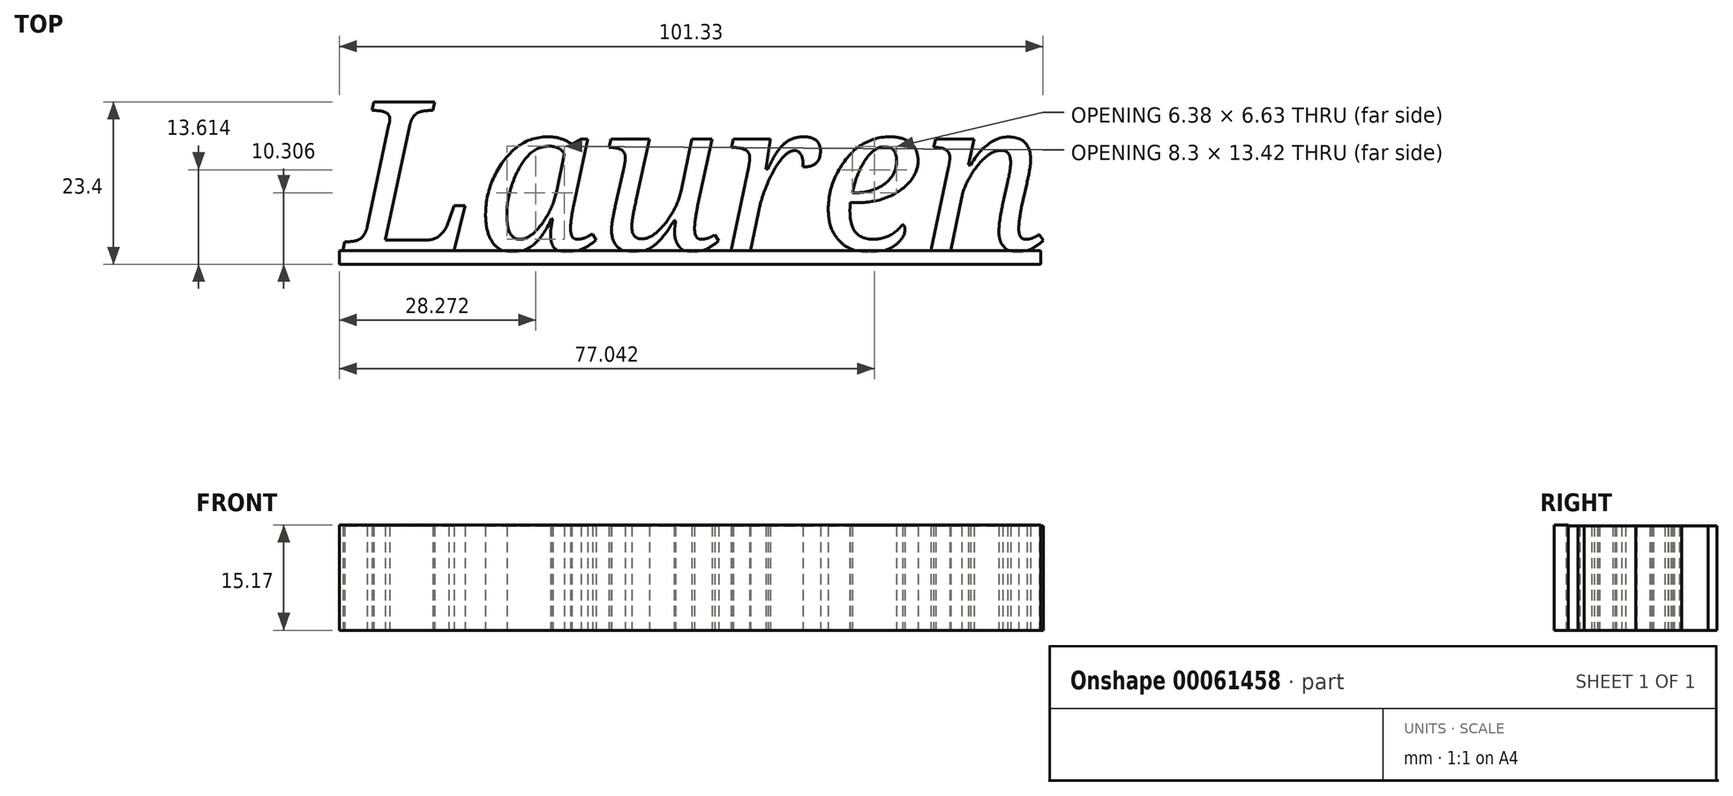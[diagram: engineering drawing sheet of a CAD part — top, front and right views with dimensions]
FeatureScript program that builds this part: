
annotation { "Feature Type Name" : "Feature", "Feature Type Description" : "" }
export const myFeature = defineFeature(function(context is Context, id is Id, definition is map)
    precondition{}
    {
        {
            var Q0;
            Q0=qCreatedBy(makeId("Top.planeOp"),FACE);
            var sketch = newSketch(context, id + "F0", { "sketchPlane" : qUnion([Q0])});
            skText(sketch, "E0", { "text": "Lauren", "fontName": "NotoSerif-Italic.ttf"});
            const initialGuessF0  = {"E0": [-0.05193, 0, 1, 0, 0.02158]};
            skSetInitialGuess(sketch, initialGuessF0);
            skSolve(sketch);
        }
        {
            var Q0;
            Q0 = qSketchRegion(id + "F0", true);
            extrude(context, id + "F1", {"entities" : qUnion([Q0]), "depth" : 15 * mm});
        }
        {
            var Q0;
            Q0=qCreatedBy(makeId("Front.planeOp"),FACE);
            var sketch = newSketch(context, id + "F2", { "sketchPlane" : qUnion([Q0])});
            skLineSegment(sketch, "E1.bottom", {"start": v(-53.03, 15.17) * mm, "end": v(47.92, 15.17) * mm});
            skLineSegment(sketch, "E1.top", {"start": v(-53.03, 0) * mm, "end": v(47.92, 0) * mm});
            skLineSegment(sketch, "E1.left", {"start": v(-53.03, 15.17) * mm, "end": v(-53.03, 0) * mm});
            skLineSegment(sketch, "E1.right", {"start": v(47.92, 15.17) * mm, "end": v(47.92, 0) * mm});
            skSolve(sketch);
        }
        {
            var Q0;
            Q0 = qSketchRegion(id + "F2", true);
            extrude(context, id + "F3", {"entities" : qUnion([Q0]), "depth" : 2 * mm});
        }
    });
